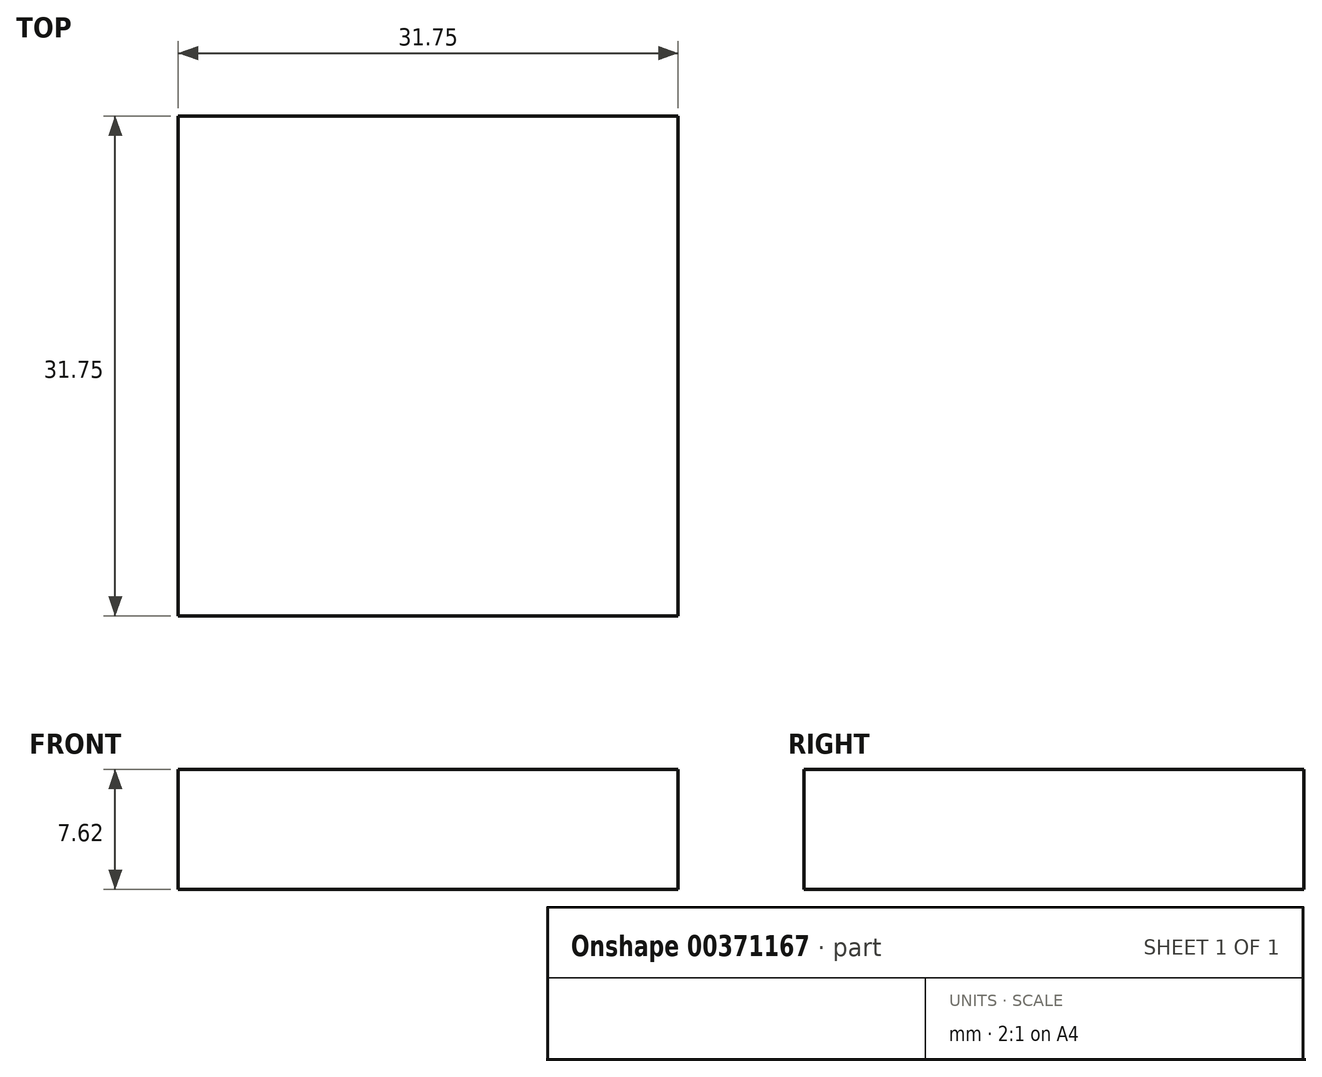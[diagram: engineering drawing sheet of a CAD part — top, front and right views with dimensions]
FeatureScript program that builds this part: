
annotation { "Feature Type Name" : "Feature", "Feature Type Description" : "" }
export const myFeature = defineFeature(function(context is Context, id is Id, definition is map)
    precondition{}
    {
        {
            var Q0;
            Q0=qCreatedBy(makeId("Top.planeOp"),FACE);
            var sketch = newSketch(context, id + "F0", { "sketchPlane" : qUnion([Q0])});
            skLineSegment(sketch, "E0.bottom", {"start": v(0, 0) * mm, "end": v(31.75, 0) * mm});
            skLineSegment(sketch, "E0.top", {"start": v(0, -31.75) * mm, "end": v(31.75, -31.75) * mm});
            skLineSegment(sketch, "E0.left", {"start": v(0, 0) * mm, "end": v(0, -31.75) * mm});
            skLineSegment(sketch, "E0.right", {"start": v(31.75, 0) * mm, "end": v(31.75, -31.75) * mm});
            skSolve(sketch);
        }
        {
            var Q0;
            Q0=makeQuery(id+"F0.imprint","IMPRINT",FACE,{"disambiguationData":[TD([[makeQuery(id+"F0.imprint","IMPRINT",EDGE,{"derivedFrom":sQuery(id+"F0.wireOp",EDGE,"E0.bottom")}),-1.0]])]});
            extrude(context, id + "F1", {"entities" : qUnion([Q0]), "depth" : 7.62 * mm});
        }
    });
